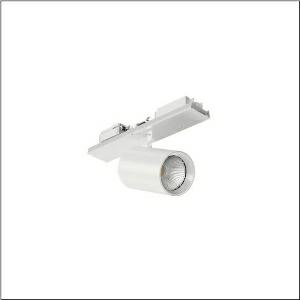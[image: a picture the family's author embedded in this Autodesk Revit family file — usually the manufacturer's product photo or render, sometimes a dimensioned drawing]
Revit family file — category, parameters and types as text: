
# Revit family: licross_r__spot_31_51sl137a43b_0799
name_source: partatom
category: Lighting Fixtures
units: mm (PartAtom-declared; Revit-internal decimal feet)

## family parameters
Cut with Voids When Loaded = No
Host = Face
Light Source = No
Part Type = Normal
Room Calculation Point = No
Round Connector Dimension = Use Diameter
Shared = No

## types (1)
- --- (1 x LED, 3680 lm, 28 W, 4000K)
    Apparent Load = 28 VA
    CIE Flux Codes = 92 97 99 100 100
    Color Rendering = 90
    Color Temperature = 4000K
    Default Elevation = 1800 mm
    Description = Licross® Spot 31, directional spotlight, light control with lens, of plastic, LED rated luminous flux: 3.680lm, light colour: 940, with plug, 3-pole, with phase selection, mains connection: 220..240V, AC, 50/60Hz, of aluminium, traffic white (RAL 9016), length: 300mm, diameter: 90mm, protection rating (complete): IP20, insulation class (complete): insulation class I (protective earthing), certification: CE, packaging unit: 1 piece
    Height = 175 mm
    Lamp = 1 x LED
    Lamp Light Flux = 3680 lm
    Lamp Power = 28 W
    Lamp count = 1
    Length = 90 mm
    Luminous efficacy = 131 lm/W
    Manufacturer = Siteco
    ModVariant = No
    Model = 51SL137A43B
    Mounting Place = Ceiling
    Mounting Type = Pendant
    Number of Poles = 1
    OnlyDefault = Yes
    Power Factor = 1
    Product Name = Licross® Spot 31
    Product group = directional spotlight
    ProductGroupID = 905
    Protection Class = Protection class I
    Protection Degree = IP 20
    RLX_Detail_Level = 1
    RLX_Emergency_Light_Flux = 0 lm
    RLX_Emergency_Type = 0
    RLX_Emergency_Type_DB = No
    RlxData = <blob elided: 14889 chars, md5=88c973da>
    Socket = socket
    Standby Power = 0 W
    System Light Flux = 3680 lm
    System Power = 28 W
    Type Comments = factory setting: luminous flux: 100 % | (ON | ON | ON) | 700 mA
    Type Image = l_1245720.jpg
    URL = http://relux.com
    VarID = @adj_153903
    Voltage = 0 V
    Weight = 0.00 kg
    Width = 0 mm  [stored 0 ft]

note: [stored X ft] marks values corroborated as IEEE doubles in the binary element streams (Revit-internal decimal feet)

## geometry (parser evidence)
native form markers: Sweep x11
no freeform markers — native parametric forms only
